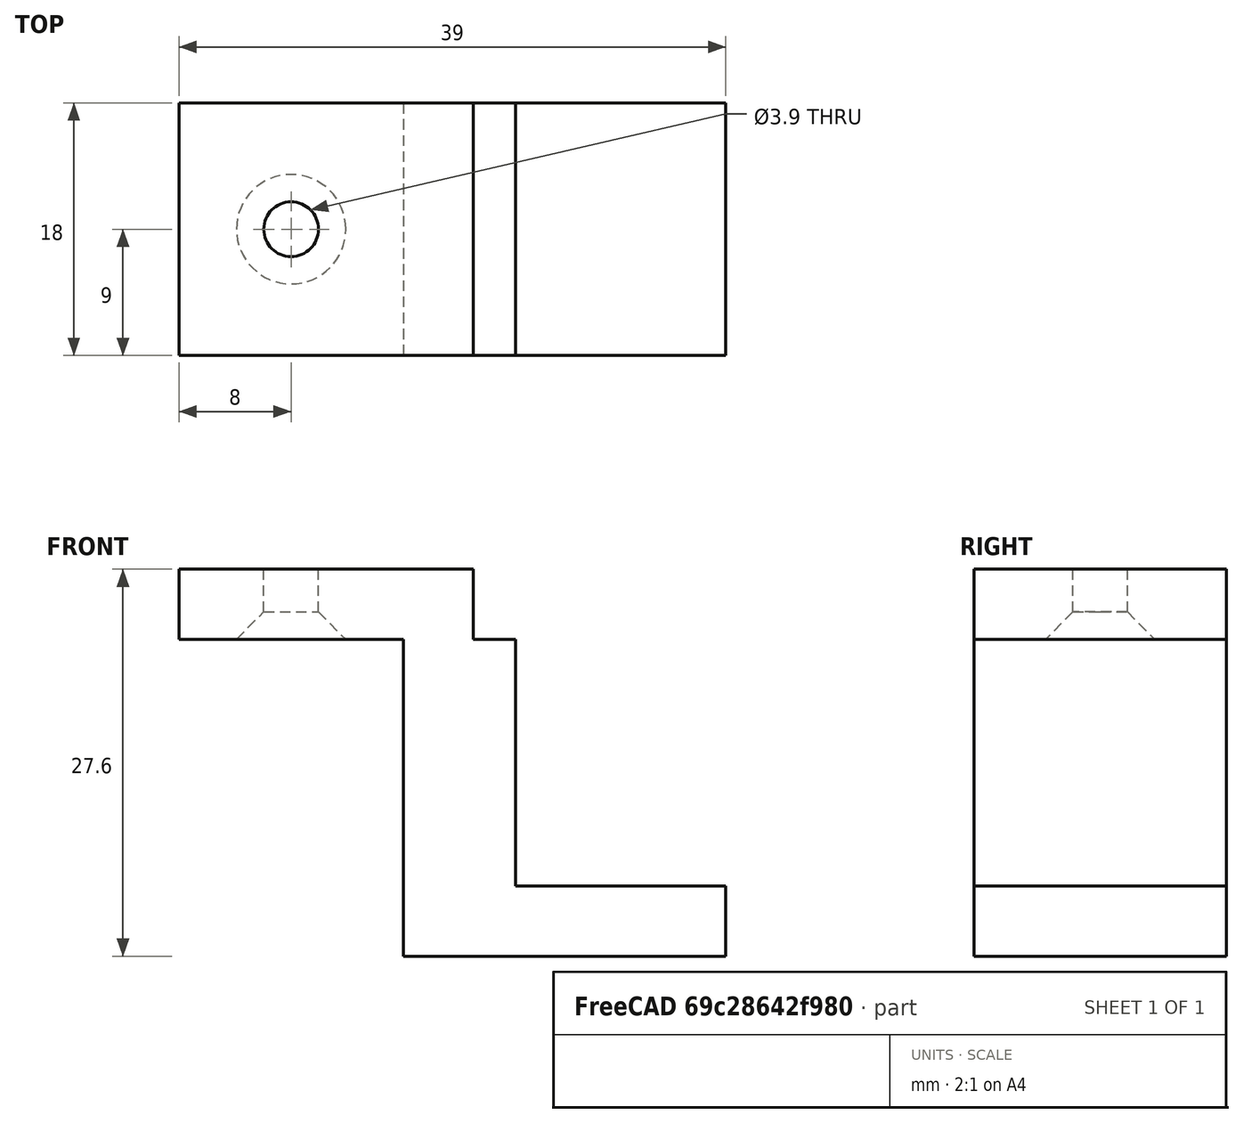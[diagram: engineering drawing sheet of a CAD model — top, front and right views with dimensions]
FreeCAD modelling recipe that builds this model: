
FCSTD DOCUMENT  (FreeCAD 0.19R24267 +99 (Git))
Label: sujeta_dvd
License: All rights reserved
LicenseURL: http://en.wikipedia.org/wiki/All_rights_reserved
objects: Sketcher::SketchObject×2, PartDesign::Pad×1, PartDesign::Hole×1, PartDesign::Body×1, Mesh::Feature×1
note: 7 computed .brp shape members not serialized (recipe doc carries the construction recipe); baked Part::Feature solids carry a one-line shape summary decoded from their .brp

FEATURE [Sketcher::SketchObject] Sketch
  FullyConstrained = true
  MapMode = 5
  Placement = pos=(0,0,0) rot=(1,0,0;1.5708rad)
  Support = -> [XZ_Plane]
  sketch-geometry (10):
    g0: LineSegment StartX=-39 StartY=27.6 StartZ=0 EndX=-18 EndY=27.6 EndZ=0
    g1: LineSegment StartX=-18 StartY=27.6 StartZ=0 EndX=-18 EndY=22.6 EndZ=0
    g2: LineSegment StartX=-18 StartY=22.6 StartZ=0 EndX=-15 EndY=22.6 EndZ=0
    g3: LineSegment StartX=-15 StartY=22.6 StartZ=0 EndX=-15 EndY=5 EndZ=0
    g4: LineSegment StartX=-15 StartY=5 StartZ=0 EndX=0 EndY=5 EndZ=0
    g5: LineSegment StartX=0 StartY=5 StartZ=0 EndX=0 EndY=0 EndZ=0
    g6: LineSegment StartX=0 StartY=0 StartZ=0 EndX=-23 EndY=0 EndZ=0
    g7: LineSegment StartX=-23 StartY=0 StartZ=0 EndX=-23 EndY=22.6 EndZ=0
    g8: LineSegment StartX=-23 StartY=22.6 StartZ=0 EndX=-39 EndY=22.6 EndZ=0
    g9: LineSegment StartX=-39 StartY=22.6 StartZ=0 EndX=-39 EndY=27.6 EndZ=0
  constraints (29):
    c: Horizontal(g0)
    c: Coincident(g0,g1)
    c: Vertical(g1)
    c: Coincident(g1,g2)
    c: Horizontal(g2)
    c: Coincident(g2,g3)
    c: Vertical(g3)
    c: Coincident(g3,g4)
    c: Horizontal(g4)
    c: Coincident(g4,g5)
    c: Vertical(g5)
    c: Coincident(g5,g6)
    c: PointOnObject(g6,g-1)
    c: Coincident(g6,g7)
    c: Vertical(g7)
    c: Coincident(g7,g8)
    c: Horizontal(g8)
    c: Coincident(g8,g9)
    c: Vertical(g9)
    c: Coincident(g0,g9)
    c: DistanceY(g1,g1) = 5
    c: DistanceY(g3,g3) = 17.6
    c: DistanceY(g5,g5) = 5
    c: DistanceX(g4,g4) = 15
    c: Coincident(g5,g-1)
    c: DistanceY(g1,g7) = 0
    c: DistanceX(g7,g0) = 5
    c: DistanceX(g8,g8) = 16
    c: DistanceX(g1,g2) = 3
FEATURE [PartDesign::Pad] Pad
  Direction = (1,1,1)
  Length = 18
  Length2 = 100
  Placement = pos=(0,0,0) rot=(1,0,0;1.5708rad)
  Profile = -> Sketch
  Type = 0
FEATURE [Sketcher::SketchObject] Sketch001
  ExternalGeometry = -> [Pad]
  FullyConstrained = false
  MapMode = 5
  Placement = pos=(0,1.51e-14,22.6) rot=(1,0,0;3.14159rad)
  Support = -> [Pad]
  sketch-geometry (1):
    g0: Circle CenterX=-31 CenterY=9 CenterZ=0 NormalX=0 NormalY=0 NormalZ=1 AngleXU=0 Radius=2.61296
  constraints (1):
    c: Symmetric(g-3,g-4,g0)
FEATURE [PartDesign::Hole] Hole
  BaseFeature = -> Pad
  Depth = 25
  DepthType = 0
  Diameter = 3.9
  DrillForDepth = false
  DrillPoint = 1
  DrillPointAngle = 118
  HoleCutCountersinkAngle = 90
  HoleCutCustomValues = false
  HoleCutDepth = 0
  HoleCutDiameter = 7.8
  HoleCutType = 4
  ModelActualThread = false
  Placement = pos=(0,0,0) rot=(1,0,0;1.5708rad)
  Profile = -> Sketch001
  Tapered = false
  TaperedAngle = 90
  ThreadAngle = 0
  ThreadClass = 0
  ThreadCutOffInner = 0
  ThreadCutOffOuter = 0
  ThreadDirection = 0
  ThreadFit = 0
  ThreadPitch = 0
  ThreadSize = 10
  ThreadType = 1
  Threaded = false
FEATURE [PartDesign::Body] Body
  Group = -> [Sketch,Pad,Sketch001,Hole]
  Origin = -> Origin
  Tip = -> Hole
FEATURE [Mesh::Feature] Mesh  label="Body (Meshed)"
